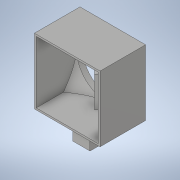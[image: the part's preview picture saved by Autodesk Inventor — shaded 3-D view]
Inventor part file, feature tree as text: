
AUTODESK INVENTOR PART (.ipt)
format: ipt  version: 2022 (Build 260153000, 153)  size: 188,928 bytes
history: native  units: in
note: dims shown in document units (in); Inventor stores cm internally (conversion verified against a paired STEP export)
features: extrude x2, sketch x2
ambient origin geometry x8: Origin, YZ Plane, XZ Plane, XY Plane, X Axis, Y Axis, Z Axis, Center Point
bodies: Solid1 (feature_tree), Body3 (feature_tree)
feature tree (4):
  extrude  "Extrusion1"  Depth=0.5118in
  extrude  "Extrusion2"  Depth=0.1181in
  sketch  "Sketch1"  dims[d0=0.3937in d1=0.0in d2=0.5118in]
  sketch  "Sketch2"  dims[d3=0.5118in d4=0.1181in d5=0.9843in d6=0.0in d7=1.9685in]
